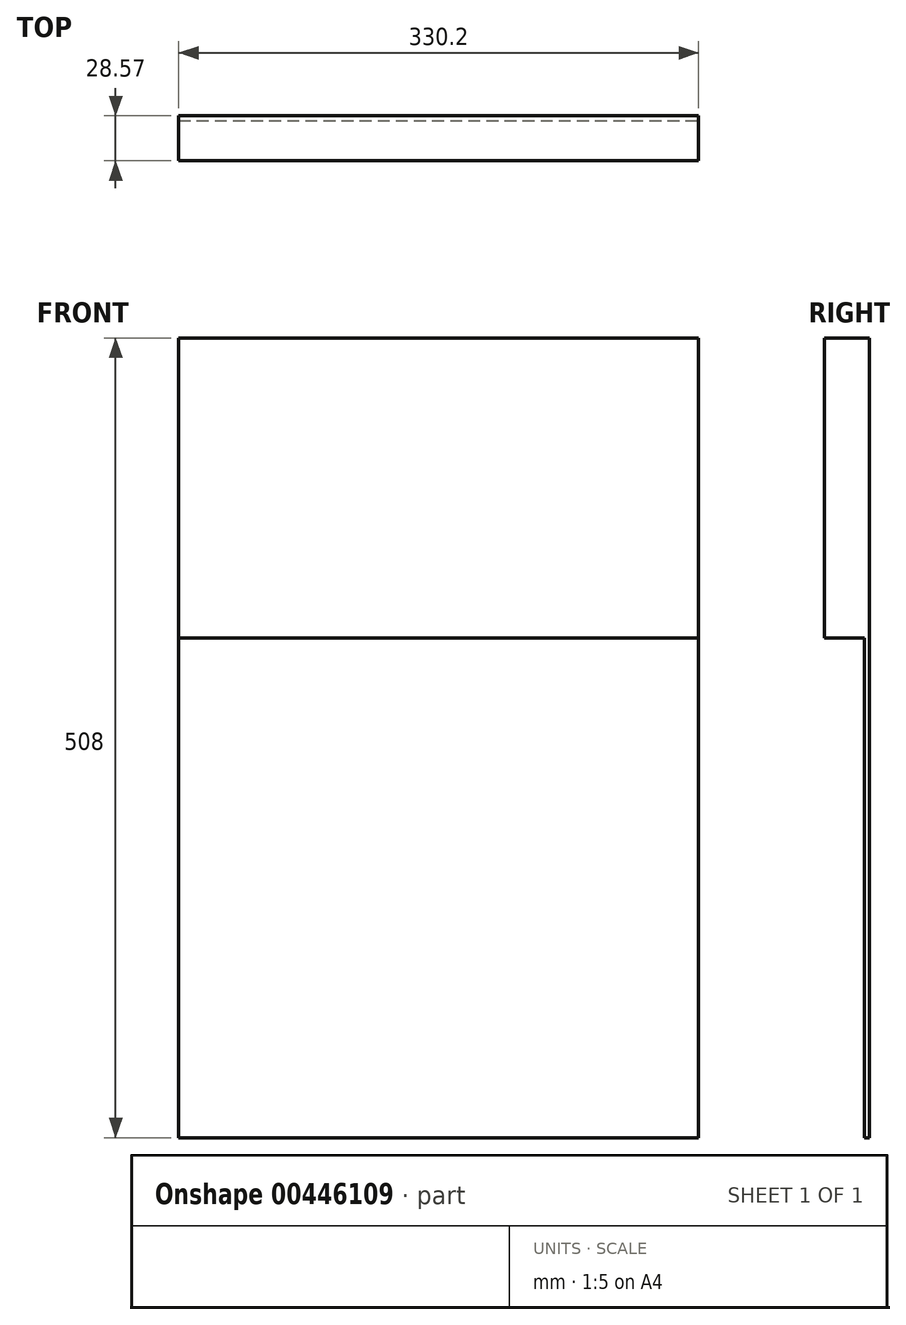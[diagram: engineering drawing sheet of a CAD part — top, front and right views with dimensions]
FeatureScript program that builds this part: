
annotation { "Feature Type Name" : "Feature", "Feature Type Description" : "" }
export const myFeature = defineFeature(function(context is Context, id is Id, definition is map)
    precondition{}
    {
        {
            var Q0;
            Q0=qCreatedBy(makeId("Front.planeOp"),FACE);
            var sketch = newSketch(context, id + "F0", { "sketchPlane" : qUnion([Q0])});
            skLineSegment(sketch, "E0.bottom", {"start": v(0, 0) * mm, "end": v(330.2, 0) * mm});
            skLineSegment(sketch, "E0.top", {"start": v(0, 317.5) * mm, "end": v(330.2, 317.5) * mm});
            skLineSegment(sketch, "E0.left", {"start": v(0, 0) * mm, "end": v(0, 317.5) * mm});
            skLineSegment(sketch, "E0.right", {"start": v(330.2, 0) * mm, "end": v(330.2, 317.5) * mm});
            skSolve(sketch);
        }
        {
            var Q0;
            Q0=makeQuery(id+"F0.imprint","IMPRINT",FACE,{"disambiguationData":[TD([[makeQuery(id+"F0.imprint","IMPRINT",EDGE,{"derivedFrom":sQuery(id+"F0.wireOp",EDGE,"E0.bottom")}),1.0]])]});
            extrude(context, id + "F1", {"entities" : qUnion([Q0]), "depth" : 3.17 * mm});
        }
        {
            var Q0;
            Q0=makeQuery(id+"F1.opExtrude","SWEPT_FACE",FACE,{"disambiguationData":[OSD([sQuery(id+"F0.wireOp",EDGE,"E0.top")])]});
            var sketch = newSketch(context, id + "F2", { "sketchPlane" : qUnion([Q0])});
            skLineSegment(sketch, "E1.bottom", {"start": v(330.2, 0) * mm, "end": v(0, 0) * mm});
            skLineSegment(sketch, "E1.top", {"start": v(330.2, -3.18) * mm, "end": v(0, -3.18) * mm});
            skLineSegment(sketch, "E1.left", {"start": v(330.2, 0) * mm, "end": v(330.2, -3.18) * mm});
            skLineSegment(sketch, "E1.right", {"start": v(0, 0) * mm, "end": v(0, -3.18) * mm});
            skSolve(sketch);
        }
        {
            var Q0;
            Q0=makeQuery(id+"F2.imprint","IMPRINT",FACE,{"disambiguationData":[TD([[makeQuery(id+"F2.imprint","IMPRINT",EDGE,{"derivedFrom":sQuery(id+"F2.wireOp",EDGE,"E1.bottom")}),-1.0]])]});
            extrude(context, id + "F3", {"entities" : qUnion([Q0]), "operationType" : NewBodyOperationType.ADD, "depth" : 190.5 * mm});
        }
        {
            var Q0;
            Q0=makeQuery(id+"F3.boolean.opBoolean","MERGE",FACE,{"derivedFrom":[makeQuery(id+"F1.opExtrude","CAP_FACE",FACE,{"disambiguationData":[OSD([sQuery(id+"F0.wireOp",EDGE,"E0.bottom"),sQuery(id+"F0.wireOp",EDGE,"E0.top"),sQuery(id+"F0.wireOp",EDGE,"E0.left"),sQuery(id+"F0.wireOp",EDGE,"E0.right")])],"isStart":false}),makeQuery(id+"F3.opExtrude","SWEPT_FACE",FACE,{"disambiguationData":[OSD([sQuery(id+"F2.wireOp",EDGE,"E1.top")])]})]});
            var sketch = newSketch(context, id + "F4", { "sketchPlane" : qUnion([Q0])});
            skLineSegment(sketch, "E2.bottom", {"start": v(0, 508) * mm, "end": v(330.2, 508) * mm});
            skLineSegment(sketch, "E2.top", {"start": v(0, 317.5) * mm, "end": v(330.2, 317.5) * mm});
            skLineSegment(sketch, "E2.left", {"start": v(0, 508) * mm, "end": v(0, 317.5) * mm});
            skLineSegment(sketch, "E2.right", {"start": v(330.2, 508) * mm, "end": v(330.2, 317.5) * mm});
            skSolve(sketch);
        }
        {
            var Q0;
            Q0=makeQuery(id+"F4.imprint","IMPRINT",FACE,{"disambiguationData":[TD([[makeQuery(id+"F4.imprint","IMPRINT",EDGE,{"derivedFrom":sQuery(id+"F4.wireOp",EDGE,"E2.bottom")}),-1.0]])]});
            extrude(context, id + "F5", {"entities" : qUnion([Q0]), "operationType" : NewBodyOperationType.ADD, "depth" : 25.4 * mm});
        }
    });
